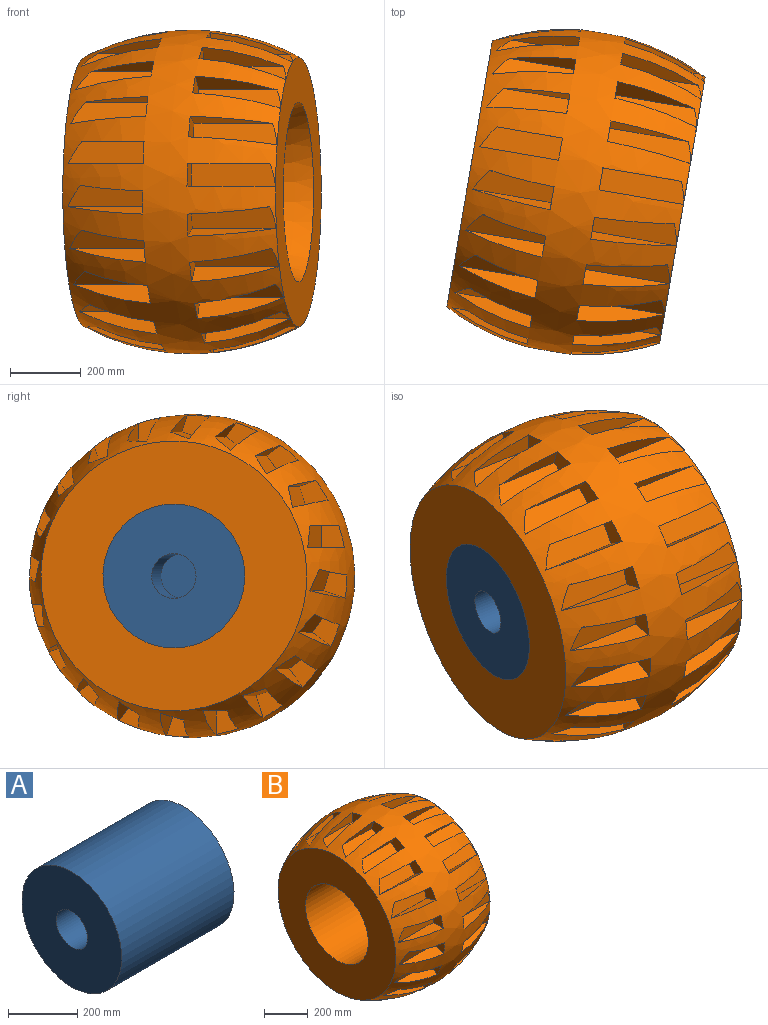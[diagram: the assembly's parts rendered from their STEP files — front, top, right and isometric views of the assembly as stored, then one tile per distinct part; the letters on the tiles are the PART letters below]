
ASSEMBLY  parts=2 mates=1
PART A: 21 faces, bbox 457.2x406.4x406.4 mm
  f0: cylinder r=203.2mm len=457.2mm, axis (-1,0,0), area 583727mm2, adj f1,f2
  f1: plane 406.4x406.4mm, normal (1,0,0), area 30402.4mm2, adj f0,f3
  f2: plane 406.4x406.4mm, normal (-1,0,0), area 117049.4mm2, adj f0,f19
  f3: cylinder r=177.8mm len=355.6mm, axis (1,0,0), area 85126.9mm2, adj f1,f4
  f4: plane 355.6x355.6mm, normal (1,0,0), area 68912.2mm2, adj f3,f5,f7,f9,f11,f13,f15,f17
  f5: cylinder r=25.4mm len=76.2mm, axis (1,0,0), area 12161mm2, adj f4,f6
  f6: plane 50.8x50.8mm, normal (1,0,0), area 2026.8mm2, adj f5
  f7: cylinder r=25.4mm len=76.2mm, axis (1,0,0), area 12161mm2, adj f4,f8
  f8: plane 50.8x50.8mm, normal (1,0,0), area 2026.8mm2, adj f7
  f9: cylinder r=25.4mm len=76.2mm, axis (1,0,0), area 12161mm2, adj f4,f10
  f10: plane 50.8x50.8mm, normal (1,0,0), area 2026.8mm2, adj f9
  f11: cylinder r=25.4mm len=76.2mm, axis (1,0,0), area 12161mm2, adj f4,f12
  f12: plane 50.8x50.8mm, normal (1,0,0), area 2026.8mm2, adj f11
  f13: cylinder r=25.4mm len=76.2mm, axis (1,0,0), area 12161mm2, adj f4,f14
  f14: plane 50.8x50.8mm, normal (1,0,0), area 2026.8mm2, adj f13
  f15: cylinder r=25.4mm len=76.2mm, axis (1,0,0), area 12161mm2, adj f4,f16
  f16: plane 50.8x50.8mm, normal (1,0,0), area 2026.8mm2, adj f15
  f17: cylinder r=76.2mm len=152.4mm, axis (-1,0,0), area 24322mm2, adj f4,f18
  f18: plane 152.4x152.4mm, normal (1,0,0), area 18241.5mm2, adj f17
  f19: cylinder r=63.5mm len=152.4mm, axis (-1,0,0), area 60804.9mm2, adj f2,f20
  f20: plane 127x127mm, normal (-1,0,0), area 12667.7mm2, adj f19
PART B: 165 faces, bbox 609.6x914.4x914.4 mm
  f0: plane 80.8x67.09mm, normal (-1,0,0), area 3732.4mm2, adj f1,f2,f3,f152
  f1: plane 186.5x47.51mm, normal (0,0.31,-0.95), area 5638.5mm2, adj f0,f3,f152
  f2: plane 225.35x62.84mm, normal (0,-0.31,0.95), area 9149.7mm2, adj f0,f3,f152
  f3: plane 225.33x60.45mm, normal (0,-0.95,-0.31), area 13216.2mm2, adj f0,f1,f2,f152
  f4: plane 82.89x82.42mm, normal (1,0,0), area 4455.3mm2, adj f5,f6,f7,f152
  f5: plane 240.7x69.28mm, normal (0,-0.31,0.95), area 10828.4mm2, adj f4,f7,f152
  f6: plane 225.35x62.84mm, normal (0,0.31,-0.95), area 9149.7mm2, adj f4,f7,f152
  f7: plane 240.66x60.41mm, normal (0,-0.95,-0.31), area 14904.8mm2, adj f4,f5,f6,f152
  f8: plane 90.18x77.7mm, normal (-1,0,0), area 3732.4mm2, adj f9,f10,f11,f152
  f9: plane 186.5x40.42mm, normal (0,0.59,-0.81), area 5638.5mm2, adj f8,f11,f152
  f10: plane 225.35x53.47mm, normal (0,-0.59,0.81), area 9149.7mm2, adj f8,f11,f152
  f11: plane 225.33x51.43mm, normal (0,-0.81,-0.59), area 13216.2mm2, adj f8,f9,f10,f152
  f12: plane 94.16x90.74mm, normal (1,0,0), area 4455.3mm2, adj f13,f14,f15,f152
  f13: plane 240.7x58.94mm, normal (0,-0.59,0.81), area 10828.4mm2, adj f12,f15,f152
  f14: plane 225.35x53.47mm, normal (0,0.59,-0.81), area 9149.7mm2, adj f12,f15,f152
  f15: plane 240.66x51.39mm, normal (0,-0.81,-0.59), area 14904.8mm2, adj f12,f13,f14,f152
  f16: plane 90.74x80.7mm, normal (-1,0,0), area 3732.4mm2, adj f17,f18,f19,f152
  f17: plane 186.5x40.42mm, normal (0,0.81,-0.59), area 5638.5mm2, adj f16,f19,f152
  f18: plane 225.35x53.47mm, normal (0,-0.81,0.59), area 9149.7mm2, adj f16,f19,f152
  f19: plane 225.33x51.43mm, normal (0,-0.59,-0.81), area 13216.2mm2, adj f16,f17,f18,f152
  f20: plane 96.21x90.18mm, normal (1,0,0), area 4455.3mm2, adj f21,f22,f23,f152
  f21: plane 240.7x58.94mm, normal (0,-0.81,0.59), area 10828.4mm2, adj f20,f23,f152
  f22: plane 225.35x53.47mm, normal (0,0.81,-0.59), area 9149.7mm2, adj f20,f23,f152
  f23: plane 240.66x51.39mm, normal (0,-0.59,-0.81), area 14904.8mm2, adj f20,f21,f22,f152
  f24: plane 82.42x75.81mm, normal (-1,0,0), area 3732.4mm2, adj f25,f26,f27,f152
  f25: plane 186.5x47.51mm, normal (0,0.95,-0.31), area 5638.5mm2, adj f24,f27,f152
  f26: plane 225.35x62.84mm, normal (0,-0.95,0.31), area 9149.7mm2, adj f24,f27,f152
  f27: plane 225.33x60.45mm, normal (0,-0.31,-0.95), area 13216.2mm2, adj f24,f25,f26,f152
  f28: plane 88.85x80.8mm, normal (1,0,0), area 4455.3mm2, adj f29,f30,f31,f152
  f29: plane 240.7x69.28mm, normal (0,-0.95,0.31), area 10828.4mm2, adj f28,f31,f152
  f30: plane 225.35x62.84mm, normal (0,0.95,-0.31), area 9149.7mm2, adj f28,f31,f152
  f31: plane 240.66x60.41mm, normal (0,-0.31,-0.95), area 14904.8mm2, adj f28,f29,f30,f152
  f32: plane 66.03x63.5mm, normal (-1,0,0), area 3732.4mm2, adj f33,f34,f35,f152
  f33: plane 186.5x49.95mm, normal (0,1,0), area 5638.5mm2, adj f32,f35,f152
  f34: plane 225.35x66.08mm, normal (0,-1,0), area 9149.7mm2, adj f32,f35,f152
  f35: plane 225.33x63.55mm, normal (0,0,-1), area 13216.2mm2, adj f32,f33,f34,f152
  f36: plane 72.79x63.5mm, normal (1,0,0), area 4455.3mm2, adj f37,f38,f39,f152
  f37: plane 240.7x72.84mm, normal (0,-1,0), area 10828.4mm2, adj f36,f39,f152
  f38: plane 225.35x66.08mm, normal (0,1,0), area 9149.7mm2, adj f36,f39,f152
  f39: plane 240.66x63.52mm, normal (0,0,-1), area 14904.8mm2, adj f36,f37,f38,f152
  f40: plane 80.8x67.09mm, normal (-1,0,0), area 3732.4mm2, adj f41,f42,f43,f152
  f41: plane 186.5x47.51mm, normal (0,0.95,0.31), area 5638.5mm2, adj f40,f43,f152
  f42: plane 225.35x62.84mm, normal (0,-0.95,-0.31), area 9149.7mm2, adj f40,f43,f152
  f43: plane 225.33x60.43mm, normal (0,0.31,-0.95), area 13216.2mm2, adj f40,f41,f42,f152
  f44: plane 82.89x82.42mm, normal (1,0,0), area 4455.3mm2, adj f45,f46,f47,f152
  f45: plane 240.7x69.28mm, normal (0,-0.95,-0.31), area 10828.4mm2, adj f44,f47,f152
  f46: plane 225.35x62.84mm, normal (0,0.95,0.31), area 9149.7mm2, adj f44,f47,f152
  f47: plane 240.66x60.41mm, normal (0,0.31,-0.95), area 14904.8mm2, adj f44,f45,f46,f152
  f48: plane 90.18x77.7mm, normal (-1,0,0), area 3732.4mm2, adj f49,f50,f51,f152
  f49: plane 186.5x40.42mm, normal (0,0.81,0.59), area 5638.5mm2, adj f48,f51,f152
  f50: plane 225.35x53.47mm, normal (0,-0.81,-0.59), area 9149.7mm2, adj f48,f51,f152
  f51: plane 225.33x51.43mm, normal (0,0.59,-0.81), area 13216.2mm2, adj f48,f49,f50,f152
  f52: plane 94.16x90.74mm, normal (1,0,0), area 4455.3mm2, adj f53,f54,f55,f152
  f53: plane 240.7x58.94mm, normal (0,-0.81,-0.59), area 10828.4mm2, adj f52,f55,f152
  f54: plane 225.35x53.47mm, normal (0,0.81,0.59), area 9149.7mm2, adj f52,f55,f152
  f55: plane 240.66x51.39mm, normal (0,0.59,-0.81), area 14904.8mm2, adj f52,f53,f54,f152
  f56: plane 90.74x80.7mm, normal (-1,0,0), area 3732.4mm2, adj f57,f58,f59,f152
  f57: plane 186.5x40.42mm, normal (0,0.59,0.81), area 5638.5mm2, adj f56,f59,f152
  f58: plane 225.35x53.47mm, normal (0,-0.59,-0.81), area 9149.7mm2, adj f56,f59,f152
  f59: plane 225.33x51.43mm, normal (0,0.81,-0.59), area 13216.2mm2, adj f56,f57,f58,f152
  f60: plane 96.21x90.18mm, normal (1,0,0), area 4455.3mm2, adj f61,f62,f63,f152
  f61: plane 240.7x58.94mm, normal (0,-0.59,-0.81), area 10828.4mm2, adj f60,f63,f152
  f62: plane 225.35x53.47mm, normal (0,0.59,0.81), area 9149.7mm2, adj f60,f63,f152
  f63: plane 240.66x51.39mm, normal (0,0.81,-0.59), area 14904.8mm2, adj f60,f61,f62,f152
  f64: plane 82.42x75.81mm, normal (-1,0,0), area 3732.4mm2, adj f65,f66,f67,f152
  f65: plane 186.5x47.51mm, normal (0,0.31,0.95), area 5638.5mm2, adj f64,f67,f152
  f66: plane 225.35x62.84mm, normal (0,-0.31,-0.95), area 9149.7mm2, adj f64,f67,f152
  f67: plane 225.33x60.45mm, normal (0,0.95,-0.31), area 13216.2mm2, adj f64,f65,f66,f152
  f68: plane 88.85x80.8mm, normal (1,0,0), area 4455.3mm2, adj f69,f70,f71,f152
  f69: plane 240.7x69.28mm, normal (0,-0.31,-0.95), area 10828.4mm2, adj f68,f71,f152
  f70: plane 225.35x62.84mm, normal (0,0.31,0.95), area 9149.7mm2, adj f68,f71,f152
  f71: plane 240.66x60.41mm, normal (0,0.95,-0.31), area 14904.8mm2, adj f68,f69,f70,f152
  f72: plane 66.03x63.5mm, normal (-1,0,0), area 3732.4mm2, adj f73,f74,f75,f152
  f73: plane 186.5x49.95mm, normal (0,0,1), area 5638.5mm2, adj f72,f75,f152
  f74: plane 225.35x66.08mm, normal (0,0,-1), area 9149.7mm2, adj f72,f75,f152
  f75: plane 225.33x63.55mm, normal (0,1,0), area 13216.2mm2, adj f72,f73,f74,f152
  f76: plane 72.79x63.5mm, normal (1,0,0), area 4455.3mm2, adj f77,f78,f79,f152
  f77: plane 240.7x72.84mm, normal (0,0,-1), area 10828.4mm2, adj f76,f79,f152
  f78: plane 225.35x66.08mm, normal (0,0,1), area 9149.7mm2, adj f76,f79,f152
  f79: plane 240.66x63.52mm, normal (0,1,0), area 14904.8mm2, adj f76,f77,f78,f152
  f80: plane 80.8x67.09mm, normal (-1,0,0), area 3732.4mm2, adj f81,f82,f83,f152
  f81: plane 186.5x47.51mm, normal (0,-0.31,0.95), area 5638.5mm2, adj f80,f83,f152
  f82: plane 225.35x62.84mm, normal (0,0.31,-0.95), area 9149.7mm2, adj f80,f83,f152
  f83: plane 225.33x60.45mm, normal (0,0.95,0.31), area 13216.2mm2, adj f80,f81,f82,f152
  f84: plane 82.89x82.42mm, normal (1,0,0), area 4455.3mm2, adj f85,f86,f87,f152
  f85: plane 240.7x69.28mm, normal (0,0.31,-0.95), area 10828.4mm2, adj f84,f87,f152
  f86: plane 225.35x62.84mm, normal (0,-0.31,0.95), area 9149.7mm2, adj f84,f87,f152
  f87: plane 240.66x60.41mm, normal (0,0.95,0.31), area 14904.8mm2, adj f84,f85,f86,f152
  f88: plane 90.18x77.7mm, normal (-1,0,0), area 3732.4mm2, adj f89,f90,f91,f152
  f89: plane 186.5x40.42mm, normal (0,-0.59,0.81), area 5638.5mm2, adj f88,f91,f152
  f90: plane 225.35x53.47mm, normal (0,0.59,-0.81), area 9149.7mm2, adj f88,f91,f152
  f91: plane 225.33x51.43mm, normal (0,0.81,0.59), area 13216.2mm2, adj f88,f89,f90,f152
  f92: plane 94.16x90.74mm, normal (1,0,0), area 4455.3mm2, adj f93,f94,f95,f152
  f93: plane 240.7x58.94mm, normal (0,0.59,-0.81), area 10828.4mm2, adj f92,f95,f152
  f94: plane 225.35x53.47mm, normal (0,-0.59,0.81), area 9149.7mm2, adj f92,f95,f152
  f95: plane 240.66x51.39mm, normal (0,0.81,0.59), area 14904.8mm2, adj f92,f93,f94,f152
  f96: plane 90.74x80.7mm, normal (-1,0,0), area 3732.4mm2, adj f97,f98,f99,f152
  f97: plane 186.5x40.42mm, normal (0,-0.81,0.59), area 5638.5mm2, adj f96,f99,f152
  f98: plane 225.35x53.47mm, normal (0,0.81,-0.59), area 9149.7mm2, adj f96,f99,f152
  f99: plane 225.33x51.43mm, normal (0,0.59,0.81), area 13216.2mm2, adj f96,f97,f98,f152
  f100: plane 96.21x90.18mm, normal (1,0,0), area 4455.3mm2, adj f101,f102,f103,f152
  f101: plane 240.7x58.94mm, normal (0,0.81,-0.59), area 10828.4mm2, adj f100,f103,f152
  f102: plane 225.35x53.47mm, normal (0,-0.81,0.59), area 9149.7mm2, adj f100,f103,f152
  f103: plane 240.66x51.39mm, normal (0,0.59,0.81), area 14904.8mm2, adj f100,f101,f102,f152
  f104: plane 82.42x75.81mm, normal (-1,0,0), area 3732.4mm2, adj f105,f106,f107,f152
  f105: plane 186.5x47.51mm, normal (0,-0.95,0.31), area 5638.5mm2, adj f104,f107,f152
  f106: plane 225.35x62.84mm, normal (0,0.95,-0.31), area 9149.7mm2, adj f104,f107,f152
  f107: plane 225.33x60.45mm, normal (0,0.31,0.95), area 13216.2mm2, adj f104,f105,f106,f152
  f108: plane 88.85x80.8mm, normal (1,0,0), area 4455.3mm2, adj f109,f110,f111,f152
  f109: plane 240.7x69.28mm, normal (0,0.95,-0.31), area 10828.4mm2, adj f108,f111,f152
  f110: plane 225.35x62.84mm, normal (0,-0.95,0.31), area 9149.7mm2, adj f108,f111,f152
  f111: plane 240.66x60.41mm, normal (0,0.31,0.95), area 14904.8mm2, adj f108,f109,f110,f152
  f112: plane 66.03x63.5mm, normal (-1,0,0), area 3732.4mm2, adj f113,f114,f115,f152
  f113: plane 186.5x49.95mm, normal (0,-1,0), area 5638.5mm2, adj f112,f115,f152
  f114: plane 225.35x66.08mm, normal (0,1,0), area 9149.7mm2, adj f112,f115,f152
  f115: plane 225.33x63.55mm, normal (0,0,1), area 13216.2mm2, adj f112,f113,f114,f152
  f116: plane 72.79x63.5mm, normal (1,0,0), area 4455.3mm2, adj f117,f118,f119,f152
  f117: plane 240.7x72.84mm, normal (0,1,0), area 10828.4mm2, adj f116,f119,f152
  f118: plane 225.35x66.08mm, normal (0,-1,0), area 9149.7mm2, adj f116,f119,f152
  f119: plane 240.66x63.52mm, normal (0,0,1), area 14904.8mm2, adj f116,f117,f118,f152
  f120: plane 80.8x67.09mm, normal (-1,0,0), area 3732.4mm2, adj f121,f122,f123,f152
  f121: plane 186.5x47.51mm, normal (0,-0.95,-0.31), area 5638.5mm2, adj f120,f123,f152
  f122: plane 225.35x62.84mm, normal (0,0.95,0.31), area 9149.7mm2, adj f120,f123,f152
  f123: plane 225.33x60.45mm, normal (0,-0.31,0.95), area 13216.2mm2, adj f120,f121,f122,f152
  f124: plane 82.89x82.42mm, normal (1,0,0), area 4455.3mm2, adj f125,f126,f127,f152
  f125: plane 240.7x69.28mm, normal (0,0.95,0.31), area 10828.4mm2, adj f124,f127,f152
  f126: plane 225.35x62.84mm, normal (0,-0.95,-0.31), area 9149.7mm2, adj f124,f127,f152
  f127: plane 240.66x60.41mm, normal (0,-0.31,0.95), area 14904.8mm2, adj f124,f125,f126,f152
  f128: plane 90.18x77.7mm, normal (-1,0,0), area 3732.4mm2, adj f129,f130,f131,f152
  f129: plane 186.5x40.42mm, normal (0,-0.81,-0.59), area 5638.5mm2, adj f128,f131,f152
  f130: plane 225.35x53.47mm, normal (0,0.81,0.59), area 9149.7mm2, adj f128,f131,f152
  f131: plane 225.33x51.43mm, normal (0,-0.59,0.81), area 13216.2mm2, adj f128,f129,f130,f152
  f132: plane 94.16x90.74mm, normal (1,0,0), area 4455.3mm2, adj f133,f134,f135,f152
  f133: plane 240.7x58.94mm, normal (0,0.81,0.59), area 10828.4mm2, adj f132,f135,f152
  f134: plane 225.35x53.47mm, normal (0,-0.81,-0.59), area 9149.7mm2, adj f132,f135,f152
  f135: plane 240.66x51.39mm, normal (0,-0.59,0.81), area 14904.8mm2, adj f132,f133,f134,f152
  f136: plane 90.74x80.7mm, normal (-1,0,0), area 3732.4mm2, adj f137,f138,f139,f152
  f137: plane 186.5x40.42mm, normal (0,-0.59,-0.81), area 5638.5mm2, adj f136,f139,f152
  f138: plane 225.35x53.47mm, normal (0,0.59,0.81), area 9149.7mm2, adj f136,f139,f152
  f139: plane 225.33x51.43mm, normal (0,-0.81,0.59), area 13216.2mm2, adj f136,f137,f138,f152
  f140: plane 96.21x90.18mm, normal (1,0,0), area 4455.3mm2, adj f141,f142,f143,f152
  f141: plane 240.7x58.94mm, normal (0,0.59,0.81), area 10828.4mm2, adj f140,f143,f152
  f142: plane 225.35x53.47mm, normal (0,-0.59,-0.81), area 9149.7mm2, adj f140,f143,f152
  f143: plane 240.66x51.39mm, normal (0,-0.81,0.59), area 14904.8mm2, adj f140,f141,f142,f152
  f144: plane 82.42x75.81mm, normal (-1,0,0), area 3732.4mm2, adj f145,f146,f147,f152
  f145: plane 186.5x47.51mm, normal (0,-0.31,-0.95), area 5638.5mm2, adj f144,f147,f152
  f146: plane 225.35x62.84mm, normal (0,0.31,0.95), area 9149.7mm2, adj f144,f147,f152
  f147: plane 225.33x60.45mm, normal (0,-0.95,0.31), area 13216.2mm2, adj f144,f145,f146,f152
  f148: plane 88.85x80.8mm, normal (1,0,0), area 4455.3mm2, adj f149,f150,f151,f152
  f149: plane 240.7x69.28mm, normal (0,0.31,0.95), area 10828.4mm2, adj f148,f151,f152
  f150: plane 225.35x62.84mm, normal (0,-0.31,-0.95), area 9149.7mm2, adj f148,f151,f152
  f151: plane 240.66x60.41mm, normal (0,-0.95,0.31), area 14904.8mm2, adj f148,f149,f150,f152
  f152: revolved ~914.4x914.4mm, area 1120938.1mm2, adj f0,f1,f2,f3,f4,f5,f6,f7
  f153: plane 762x762mm, normal (-1,0,0), area 326319.6mm2, adj f152,f154
  f154: cylinder r=203.2mm len=457.2mm, axis (1,0,0), area 583727mm2, adj f153,f156
  f155: plane 762x762mm, normal (1,0,0), area 253353.7mm2, adj f152,f156
  f156: cone r=203.2mm half-angle=18.4deg, axis (1,0,0), area 230738.4mm2, adj f154,f155
  f157: plane 72.79x63.5mm, normal (1,0,0), area 4455.3mm2, adj f152,f158,f159,f160
  f158: plane 240.7x72.84mm, normal (0,0,1), area 10828.4mm2, adj f152,f157,f160
  f159: plane 225.35x66.08mm, normal (0,0,-1), area 9149.7mm2, adj f152,f157,f160
  f160: plane 240.66x63.52mm, normal (0,-1,0), area 14904.8mm2, adj f152,f157,f158,f159
  f161: plane 66.03x63.5mm, normal (-1,0,0), area 3732.4mm2, adj f152,f162,f163,f164
  f162: plane 186.5x49.95mm, normal (0,0,-1), area 5638.5mm2, adj f152,f161,f164
  f163: plane 225.35x66.08mm, normal (0,0,1), area 9149.7mm2, adj f152,f161,f164
  f164: plane 225.33x63.55mm, normal (0,-1,0), area 13216.2mm2, adj f152,f161,f162,f163
PLACE A rot(axis=(0,0,-1),9.7deg) t=(-1399.42,1030.8,-410.09)mm
PLACE B rot(axis=(0,0,-1),9.7deg) t=(-1099.01,979.26,-117.99)mm
MATE fastened A.f0 <-> B.f156  axis (-0.99,0.17,0) through (-1399.42,1030.8,-410.09)mm
